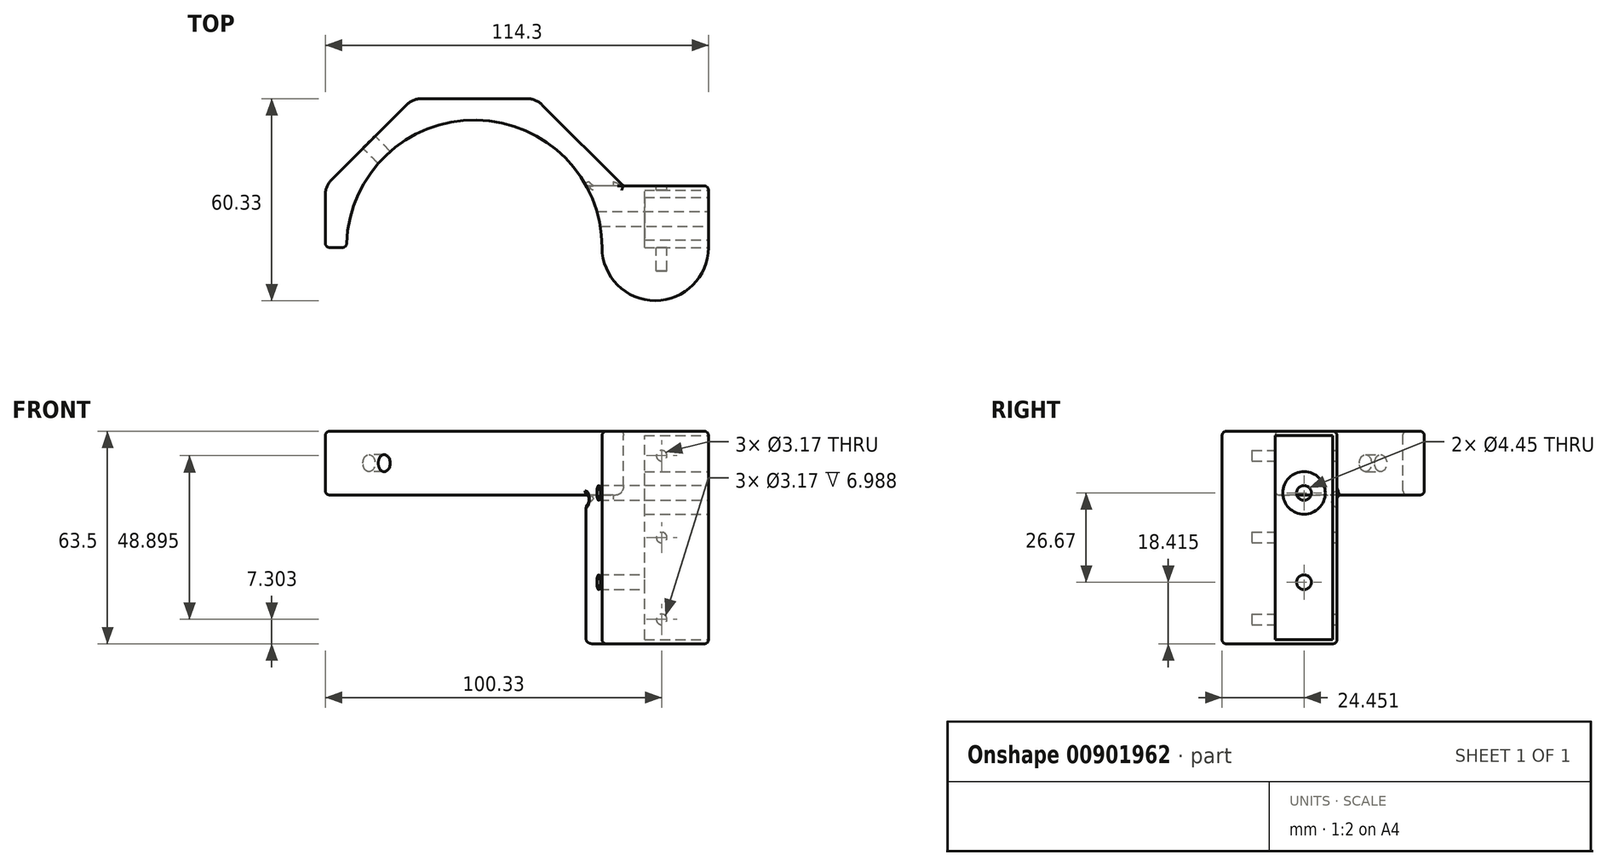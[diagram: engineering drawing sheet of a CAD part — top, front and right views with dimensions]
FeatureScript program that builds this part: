
annotation { "Feature Type Name" : "Feature", "Feature Type Description" : "" }
export const myFeature = defineFeature(function(context is Context, id is Id, definition is map)
    precondition{}
    {
        {
            var Q0;
            Q0=qCreatedBy(makeId("Top.planeOp"),FACE);
            var sketch = newSketch(context, id + "F0", { "sketchPlane" : qUnion([Q0])});
            skArc(sketch, "E0", {"start": v(38.1, 0) * mm, "mid": v(0, 38.1) * mm, "end": v(-38.1, 0) * mm});
            skCircle(sketch, "E1.cCircle", {"center": v(0, 0) * mm, "radius": 44.45 * mm, "construction": true});
            skLineSegment(sketch, "E1.0", {"start": v(44.45, 18.41) * mm, "end": v(44.45, 0) * mm});
            skLineSegment(sketch, "E1.4", {"start": v(-44.45, 0) * mm, "end": v(-44.45, 18.41) * mm});
            skLineSegment(sketch, "E1.5", {"start": v(-44.45, 18.41) * mm, "end": v(-18.41, 44.45) * mm});
            skLineSegment(sketch, "E1.6", {"start": v(-18.41, 44.45) * mm, "end": v(18.41, 44.45) * mm});
            skLineSegment(sketch, "E1.7", {"start": v(18.41, 44.45) * mm, "end": v(44.45, 18.41) * mm});
            skPoint(sketch, "E1.0.midPoint", {"position": v(44.45, 0) * mm});
            skLineSegment(sketch, "E2", {"start": v(-44.45, 0) * mm, "end": v(-38.1, 0) * mm});
            skPoint(sketch, "E3.orphan", {"position": v(-44.45, -18.41) * mm});
            skPoint(sketch, "E4.orphan", {"position": v(44.45, -18.41) * mm});
            skLineSegment(sketch, "E5.trimOffspring", {"start": v(38.1, 0) * mm, "end": v(44.45, 0) * mm});
            skLineSegment(sketch, "E6", {"start": v(44.45, 0) * mm, "end": v(69.85, 0) * mm});
            skLineSegment(sketch, "E7", {"start": v(69.85, 0) * mm, "end": v(69.85, 18.41) * mm});
            skLineSegment(sketch, "E8", {"start": v(69.85, 18.41) * mm, "end": v(44.45, 18.41) * mm});
            skArc(sketch, "E9", {"start": v(38.1, 0) * mm, "mid": v(53.98, -15.88) * mm, "end": v(69.85, 0) * mm});
            skLineSegment(sketch, "E10", {"start": v(44.45, 18.41) * mm, "end": v(33.36, 18.41) * mm});
            skSolve(sketch);
        }
        {
            var Q0;
            Q0=makeQuery(id+"F0.imprint","IMPRINT",FACE,{"disambiguationData":[TD([[makeQuery(id+"F0.imprint","IMPRINT",EDGE,{"derivedFrom":sQuery(id+"F0.wireOp",EDGE,"E1.0")}),1.0]])]});
            var Q1;
            Q1=makeQuery(id+"F0.imprint","IMPRINT",FACE,{"disambiguationData":[TD([[makeQuery(id+"F0.imprint","IMPRINT",EDGE,{"derivedFrom":sQuery(id+"F0.wireOp",EDGE,"E5.trimOffspring")}),-1.0]])]});
            var Q2;
            Q2=makeQuery(id+"F0.imprint","IMPRINT",FACE,{"disambiguationData":[TD([[makeQuery(id+"F0.imprint","IMPRINT",EDGE,{"derivedFrom":sQuery(id+"F0.wireOp",EDGE,"E1.0")}),-1.0]])]});
            extrude(context, id + "F1", {"entities" : qUnion([Q0, Q1, Q2]), "oppositeDirection" : true, "depth" : 63.5 * mm, "offsetDistance" : 25.4 * mm});
        }
        {
            var Q0;
            Q0=makeQuery(id+"F0.imprint","IMPRINT",FACE,{"disambiguationData":[TD([[makeQuery(id+"F0.imprint","IMPRINT",EDGE,{"derivedFrom":sQuery(id+"F0.wireOp",EDGE,"E1.4")}),-1.0]])]});
            extrude(context, id + "F2", {"entities" : qUnion([Q0]), "operationType" : NewBodyOperationType.ADD, "oppositeDirection" : true, "depth" : 19.05 * mm, "offsetDistance" : 25.4 * mm});
        }
        {
            var Q0;
            Q0=makeQuery(id+"F2.opExtrude","SWEPT_EDGE",EDGE,{"disambiguationData":[OSD([sQuery(id+"F0.wireOp",EDGE,"E1.0"),sQuery(id+"F0.wireOp",EDGE,"E1.7"),sQuery(id+"F0.wireOp",EDGE,"E8"),sQuery(id+"F0.wireOp",EDGE,"E10")])]});
            var Q1;
            Q1=makeQuery(id+"F2.opExtrude","SWEPT_EDGE",EDGE,{"disambiguationData":[OSD([sQuery(id+"F0.wireOp",EDGE,"E1.6"),sQuery(id+"F0.wireOp",EDGE,"E1.7")])]});
            var Q2;
            Q2=makeQuery(id+"F2.opExtrude","SWEPT_EDGE",EDGE,{"disambiguationData":[OSD([sQuery(id+"F0.wireOp",EDGE,"E1.5"),sQuery(id+"F0.wireOp",EDGE,"E1.6")])]});
            var Q3;
            Q3=makeQuery(id+"F2.opExtrude","SWEPT_EDGE",EDGE,{"disambiguationData":[OSD([sQuery(id+"F0.wireOp",EDGE,"E1.4"),sQuery(id+"F0.wireOp",EDGE,"E1.5")])]});
            var Q4;
            Q4=makeQuery(id+"F2.opExtrude","CAP_EDGE",EDGE,{"disambiguationData":[OSD([sQuery(id+"F0.wireOp",EDGE,"E10")])],"isStart":false});
            fillet(context, id + "F3", {"entities" : qUnion([Q0, Q1, Q2, Q3, Q4]), "radius" : 6.35 * mm, "tangentPropagation" : true, "allowEdgeOverflow" : false});
        }
        {
            var Q0;
            Q0=makeQuery(id+"F1.opExtrude","SWEPT_EDGE",EDGE,{"disambiguationData":[OSD([sQuery(id+"F0.wireOp",EDGE,"E7"),sQuery(id+"F0.wireOp",EDGE,"E8")])]});
            var Q1;
            {var subQ0=sQuery(id+"F0.wireOp",EDGE,"E10");var subQ1=sQuery(id+"F0.wireOp",EDGE,"E0");Q1=makeQuery(id+"F2.boolean.opBoolean","MERGE",FACE,{"derivedFrom":[makeQuery(id+"F1.opExtrude","CAP_FACE",FACE,{"disambiguationData":[OSD([subQ1,sQuery(id+"F0.wireOp",EDGE,"E7"),sQuery(id+"F0.wireOp",EDGE,"E8"),sQuery(id+"F0.wireOp",EDGE,"E9"),subQ0])],"isStart":true}),makeQuery(id+"F2.opExtrude","CAP_FACE",FACE,{"disambiguationData":[OSD([subQ1,sQuery(id+"F0.wireOp",EDGE,"E1.4"),sQuery(id+"F0.wireOp",EDGE,"E1.5"),sQuery(id+"F0.wireOp",EDGE,"E1.6"),sQuery(id+"F0.wireOp",EDGE,"E1.7"),sQuery(id+"F0.wireOp",EDGE,"E2"),subQ0])],"isStart":true})]});}
            var Q2;
            Q2=makeQuery(id+"F2.opExtrude","SWEPT_FACE",FACE,{"disambiguationData":[OSD([sQuery(id+"F0.wireOp",EDGE,"E2")])]});
            var Q3;
            Q3=makeQuery(id+"F2.opExtrude","CAP_FACE",FACE,{"disambiguationData":[OSD([sQuery(id+"F0.wireOp",EDGE,"E0"),sQuery(id+"F0.wireOp",EDGE,"E1.4"),sQuery(id+"F0.wireOp",EDGE,"E1.5"),sQuery(id+"F0.wireOp",EDGE,"E1.6"),sQuery(id+"F0.wireOp",EDGE,"E1.7"),sQuery(id+"F0.wireOp",EDGE,"E2"),sQuery(id+"F0.wireOp",EDGE,"E10")])],"isStart":false});
            var Q4;
            Q4=makeQuery(id+"F1.opExtrude","CAP_FACE",FACE,{"disambiguationData":[OSD([sQuery(id+"F0.wireOp",EDGE,"E0"),sQuery(id+"F0.wireOp",EDGE,"E7"),sQuery(id+"F0.wireOp",EDGE,"E8"),sQuery(id+"F0.wireOp",EDGE,"E9"),sQuery(id+"F0.wireOp",EDGE,"E10")])],"isStart":false});
            fillet(context, id + "F4", {"entities" : qUnion([Q0, Q1, Q2, Q3, Q4]), "radius" : 1.27 * mm, "tangentPropagation" : true, "allowEdgeOverflow" : false});
        }
        {
            var Q0;
            Q0=makeQuery(id+"F2.opExtrude","SWEPT_FACE",FACE,{"disambiguationData":[OSD([sQuery(id+"F0.wireOp",EDGE,"E1.5")])]});
            var sketch = newSketch(context, id + "F5", { "sketchPlane" : qUnion([Q0])});
            skLineSegment(sketch, "E11", {"start": v(15.78, -1.27) * mm, "end": v(-15.78, -17.78) * mm});
            skCircle(sketch, "E12", {"center": v(0, -9.52) * mm, "radius": 2.54 * mm});
            skSolve(sketch);
        }
        {
            var Q0;
            {var subQ0=sQuery(id+"F5.wireOp",EDGE,"E12");var subQ1=sQuery(id+"F5.wireOp",EDGE,"E11");var subQ2=makeQuery(id+"F5.imprint","INTERSECT",VERTEX,{"disambiguationData":[OD(0.0)],"derivedFrom":[subQ1,subQ0]});Q0=makeQuery(id+"F5.imprint","IMPRINT",FACE,{"disambiguationData":[TD([[makeQuery(id+"F5.imprint","IMPRINT",EDGE,{"disambiguationData":[TD([[subQ2,-1.0]])],"derivedFrom":subQ1}),-1.0]])]});}
            var Q1;
            {var subQ0=sQuery(id+"F5.wireOp",EDGE,"E12");var subQ1=sQuery(id+"F5.wireOp",EDGE,"E11");var subQ2=makeQuery(id+"F5.imprint","INTERSECT",VERTEX,{"disambiguationData":[OD(0.0)],"derivedFrom":[subQ1,subQ0]});Q1=makeQuery(id+"F5.imprint","IMPRINT",FACE,{"disambiguationData":[TD([[makeQuery(id+"F5.imprint","IMPRINT",EDGE,{"disambiguationData":[TD([[subQ2,-1.0]])],"derivedFrom":subQ1}),1.0]])]});}
            extrude(context, id + "F6", {"entities" : qUnion([Q0, Q1]), "operationType" : NewBodyOperationType.REMOVE, "oppositeDirection" : true, "depth" : 25.4 * mm, "offsetDistance" : 25.4 * mm});
        }
        {
            var Q0;
            Q0=makeQuery(id+"F1.opExtrude","SWEPT_FACE",FACE,{"disambiguationData":[OSD([sQuery(id+"F0.wireOp",EDGE,"E8"),sQuery(id+"F0.wireOp",EDGE,"E10")])]});
            var sketch = newSketch(context, id + "F7", { "sketchPlane" : qUnion([Q0])});
            skLineSegment(sketch, "E13", {"start": v(-68.58, -7.3) * mm, "end": v(-68.58, -56.2) * mm});
            skLineSegment(sketch, "E14.0", {"start": v(-55.88, -7.3) * mm, "end": v(-55.88, -56.2) * mm});
            skCircle(sketch, "E15", {"center": v(-55.88, -7.3) * mm, "radius": 1.59 * mm});
            skCircle(sketch, "E16", {"center": v(-55.88, -31.75) * mm, "radius": 1.59 * mm});
            skCircle(sketch, "E17", {"center": v(-55.88, -56.2) * mm, "radius": 1.59 * mm});
            skSolve(sketch);
        }
        {
            var Q0;
            Q0=makeQuery(id+"F7.imprint","IMPRINT",FACE,{"disambiguationData":[TD([[makeQuery(id+"F7.imprint","IMPRINT",EDGE,{"derivedFrom":sQuery(id+"F7.wireOp",EDGE,"E15")}),1.0]])]});
            var Q1;
            {var subQ0=sQuery(id+"F7.wireOp",EDGE,"E16");var subQ1=sQuery(id+"F7.wireOp",EDGE,"E14.0");var subQ2=makeQuery(id+"F7.imprint","INTERSECT",VERTEX,{"disambiguationData":[OD(0.0)],"derivedFrom":[subQ1,subQ0]});Q1=makeQuery(id+"F7.imprint","IMPRINT",FACE,{"disambiguationData":[TD([[makeQuery(id+"F7.imprint","IMPRINT",EDGE,{"disambiguationData":[TD([[subQ2,1.0]])],"derivedFrom":subQ1}),1.0]])]});}
            var Q2;
            {var subQ0=sQuery(id+"F7.wireOp",EDGE,"E16");var subQ1=sQuery(id+"F7.wireOp",EDGE,"E14.0");var subQ2=makeQuery(id+"F7.imprint","INTERSECT",VERTEX,{"disambiguationData":[OD(0.0)],"derivedFrom":[subQ1,subQ0]});Q2=makeQuery(id+"F7.imprint","IMPRINT",FACE,{"disambiguationData":[TD([[makeQuery(id+"F7.imprint","IMPRINT",EDGE,{"disambiguationData":[TD([[subQ2,1.0]])],"derivedFrom":subQ1}),-1.0]])]});}
            var Q3;
            Q3=makeQuery(id+"F7.imprint","IMPRINT",FACE,{"disambiguationData":[TD([[makeQuery(id+"F7.imprint","IMPRINT",EDGE,{"derivedFrom":sQuery(id+"F7.wireOp",EDGE,"E17")}),1.0]])]});
            extrude(context, id + "F8", {"entities" : qUnion([Q0, Q1, Q2, Q3]), "operationType" : NewBodyOperationType.REMOVE, "oppositeDirection" : true, "depth" : 25.4 * mm, "offsetDistance" : 25.4 * mm});
        }
        {
            var Q0;
            Q0=makeQuery(id+"F1.opExtrude","SWEPT_FACE",FACE,{"disambiguationData":[OSD([sQuery(id+"F0.wireOp",EDGE,"E7")])]});
            var sketch = newSketch(context, id + "F9", { "sketchPlane" : qUnion([Q0])});
            skLineSegment(sketch, "E18", {"start": v(8.57, -1.27) * mm, "end": v(8.57, -62.23) * mm});
            skCircle(sketch, "E19", {"center": v(8.57, -45.09) * mm, "radius": 2.22 * mm});
            skCircle(sketch, "E20", {"center": v(8.57, -18.42) * mm, "radius": 2.22 * mm});
            skCircle(sketch, "E21", {"center": v(8.57, -45.09) * mm, "radius": 6.35 * mm});
            skCircle(sketch, "E22", {"center": v(8.57, -18.42) * mm, "radius": 6.35 * mm});
            skSolve(sketch);
        }
        {
            var Q0;
            {var subQ0=sQuery(id+"F9.wireOp",EDGE,"E19");var subQ1=sQuery(id+"F9.wireOp",EDGE,"E18");var subQ2=makeQuery(id+"F9.imprint","INTERSECT",VERTEX,{"disambiguationData":[OD(0.0)],"derivedFrom":[subQ1,subQ0]});Q0=makeQuery(id+"F9.imprint","IMPRINT",FACE,{"disambiguationData":[TD([[makeQuery(id+"F9.imprint","IMPRINT",EDGE,{"disambiguationData":[TD([[subQ2,-1.0]])],"derivedFrom":subQ1}),1.0]])]});}
            var Q1;
            {var subQ0=sQuery(id+"F9.wireOp",EDGE,"E19");var subQ1=sQuery(id+"F9.wireOp",EDGE,"E18");var subQ2=makeQuery(id+"F9.imprint","INTERSECT",VERTEX,{"disambiguationData":[OD(0.0)],"derivedFrom":[subQ1,subQ0]});Q1=makeQuery(id+"F9.imprint","IMPRINT",FACE,{"disambiguationData":[TD([[makeQuery(id+"F9.imprint","IMPRINT",EDGE,{"disambiguationData":[TD([[subQ2,-1.0]])],"derivedFrom":subQ1}),-1.0]])]});}
            var Q2;
            {var subQ0=sQuery(id+"F9.wireOp",EDGE,"E20");var subQ1=sQuery(id+"F9.wireOp",EDGE,"E18");var subQ2=makeQuery(id+"F9.imprint","INTERSECT",VERTEX,{"disambiguationData":[OD(0.0)],"derivedFrom":[subQ1,subQ0]});Q2=makeQuery(id+"F9.imprint","IMPRINT",FACE,{"disambiguationData":[TD([[makeQuery(id+"F9.imprint","IMPRINT",EDGE,{"disambiguationData":[TD([[subQ2,-1.0]])],"derivedFrom":subQ1}),1.0]])]});}
            var Q3;
            {var subQ0=sQuery(id+"F9.wireOp",EDGE,"E20");var subQ1=sQuery(id+"F9.wireOp",EDGE,"E18");var subQ2=makeQuery(id+"F9.imprint","INTERSECT",VERTEX,{"disambiguationData":[OD(0.0)],"derivedFrom":[subQ1,subQ0]});Q3=makeQuery(id+"F9.imprint","IMPRINT",FACE,{"disambiguationData":[TD([[makeQuery(id+"F9.imprint","IMPRINT",EDGE,{"disambiguationData":[TD([[subQ2,-1.0]])],"derivedFrom":subQ1}),-1.0]])]});}
            extrude(context, id + "F10", {"entities" : qUnion([Q0, Q1, Q2, Q3]), "operationType" : NewBodyOperationType.REMOVE, "oppositeDirection" : true, "depth" : 76.2 * mm, "offsetDistance" : 25.4 * mm});
        }
        {
            var Q0;
            {var subQ0=sQuery(id+"F9.wireOp",EDGE,"E21");var subQ1=sQuery(id+"F9.wireOp",EDGE,"E18");var subQ2=makeQuery(id+"F9.imprint","INTERSECT",VERTEX,{"disambiguationData":[OD(0.0)],"derivedFrom":[subQ1,subQ0]});Q0=makeQuery(id+"F9.imprint","IMPRINT",FACE,{"disambiguationData":[TD([[makeQuery(id+"F9.imprint","IMPRINT",EDGE,{"disambiguationData":[TD([[subQ2,-1.0]])],"derivedFrom":subQ1}),1.0]])]});}
            var Q1;
            {var subQ0=sQuery(id+"F9.wireOp",EDGE,"E21");var subQ1=sQuery(id+"F9.wireOp",EDGE,"E18");var subQ2=makeQuery(id+"F9.imprint","INTERSECT",VERTEX,{"disambiguationData":[OD(0.0)],"derivedFrom":[subQ1,subQ0]});Q1=makeQuery(id+"F9.imprint","IMPRINT",FACE,{"disambiguationData":[TD([[makeQuery(id+"F9.imprint","IMPRINT",EDGE,{"disambiguationData":[TD([[subQ2,-1.0]])],"derivedFrom":subQ1}),-1.0]])]});}
            var Q2;
            {var subQ0=sQuery(id+"F9.wireOp",EDGE,"E22");var subQ1=sQuery(id+"F9.wireOp",EDGE,"E18");var subQ2=makeQuery(id+"F9.imprint","INTERSECT",VERTEX,{"disambiguationData":[OD(0.0)],"derivedFrom":[subQ1,subQ0]});Q2=makeQuery(id+"F9.imprint","IMPRINT",FACE,{"disambiguationData":[TD([[makeQuery(id+"F9.imprint","IMPRINT",EDGE,{"disambiguationData":[TD([[subQ2,-1.0]])],"derivedFrom":subQ1}),1.0]])]});}
            var Q3;
            {var subQ0=sQuery(id+"F9.wireOp",EDGE,"E22");var subQ1=sQuery(id+"F9.wireOp",EDGE,"E18");var subQ2=makeQuery(id+"F9.imprint","INTERSECT",VERTEX,{"disambiguationData":[OD(0.0)],"derivedFrom":[subQ1,subQ0]});Q3=makeQuery(id+"F9.imprint","IMPRINT",FACE,{"disambiguationData":[TD([[makeQuery(id+"F9.imprint","IMPRINT",EDGE,{"disambiguationData":[TD([[subQ2,-1.0]])],"derivedFrom":subQ1}),-1.0]])]});}
            extrude(context, id + "F11", {"entities" : qUnion([Q0, Q1, Q2, Q3]), "operationType" : NewBodyOperationType.REMOVE, "oppositeDirection" : true, "depth" : 19.05 * mm, "offsetDistance" : 25.4 * mm});
        }
    });
